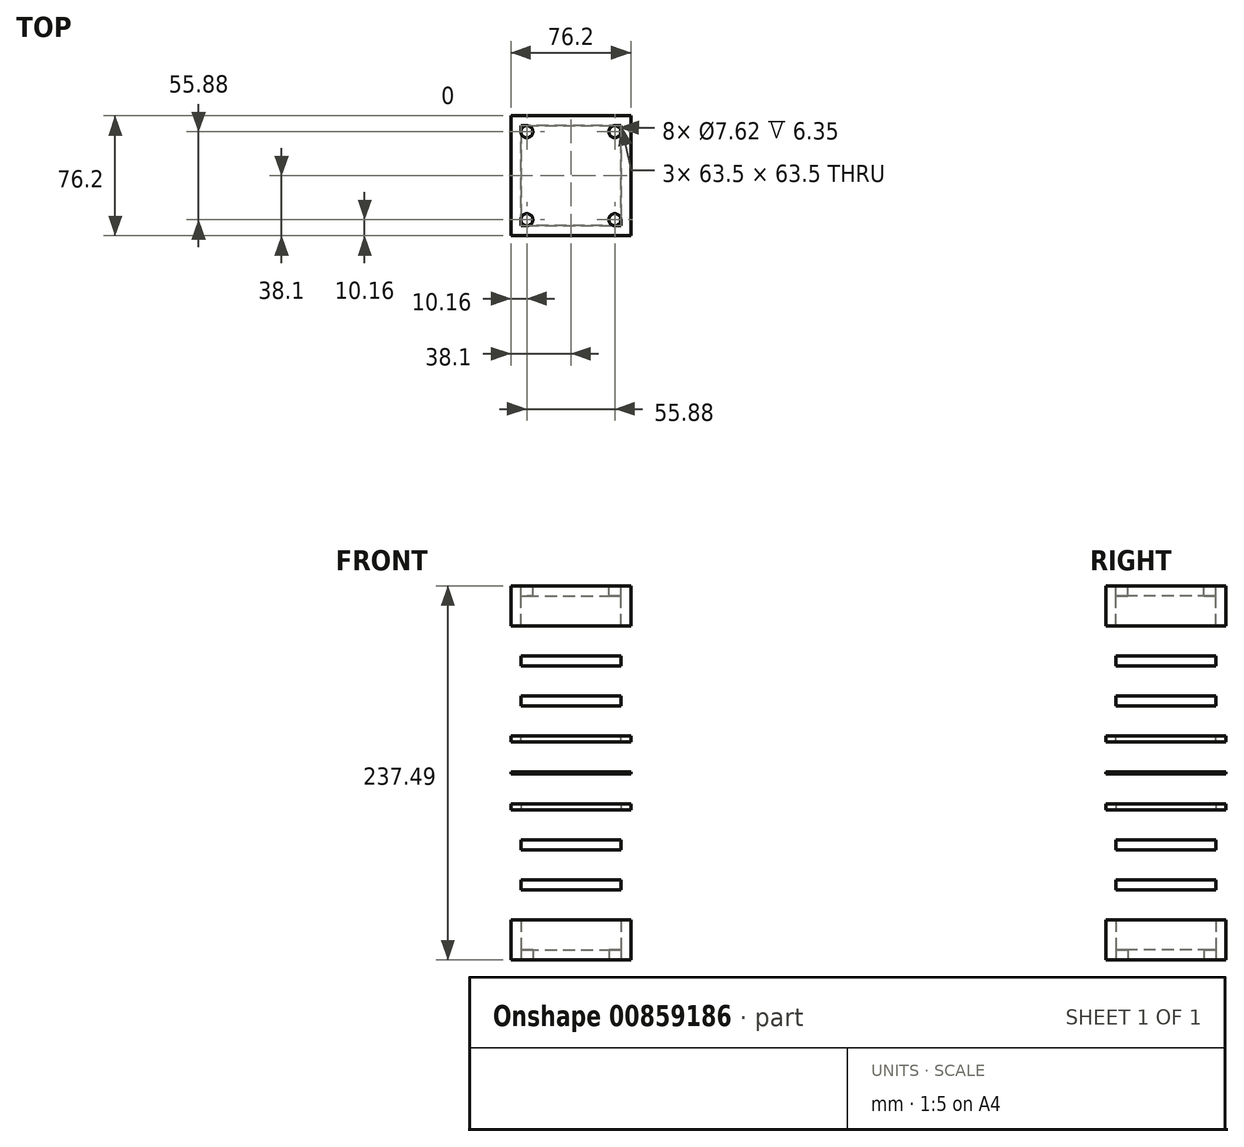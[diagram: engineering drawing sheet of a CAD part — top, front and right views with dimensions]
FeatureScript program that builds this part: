
annotation { "Feature Type Name" : "Feature", "Feature Type Description" : "" }
export const myFeature = defineFeature(function(context is Context, id is Id, definition is map)
    precondition{}
    {
        {
            var Q0;
            Q0=qCreatedBy(makeId("Top.planeOp"),FACE);
            var sketch = newSketch(context, id + "F0", { "sketchPlane" : qUnion([Q0])});
            skLineSegment(sketch, "E0.bottom", {"start": v(0, 0) * mm, "end": v(76.2, 0) * mm});
            skLineSegment(sketch, "E0.top", {"start": v(0, 76.2) * mm, "end": v(76.2, 76.2) * mm});
            skLineSegment(sketch, "E0.left", {"start": v(0, 0) * mm, "end": v(0, 76.2) * mm});
            skLineSegment(sketch, "E0.right", {"start": v(76.2, 0) * mm, "end": v(76.2, 76.2) * mm});
            skLineSegment(sketch, "E1.bottom", {"start": v(6.35, 69.85) * mm, "end": v(69.85, 69.85) * mm});
            skLineSegment(sketch, "E1.top", {"start": v(6.35, 6.35) * mm, "end": v(69.85, 6.35) * mm});
            skLineSegment(sketch, "E1.left", {"start": v(6.35, 69.85) * mm, "end": v(6.35, 6.35) * mm});
            skLineSegment(sketch, "E1.right", {"start": v(69.85, 69.85) * mm, "end": v(69.85, 6.35) * mm});
            skSolve(sketch);
        }
        {
            var Q0;
            Q0 = qSketchRegion(id + "F0", true);
            extrude(context, id + "F1", {"entities" : qUnion([Q0]), "depth" : 25.4 * mm, "offsetDistance" : 25.4 * mm});
        }
        {
            var Q0;
            Q0=makeQuery(id+"F0.imprint","IMPRINT",FACE,{"disambiguationData":[TD([[makeQuery(id+"F0.imprint","IMPRINT",EDGE,{"derivedFrom":sQuery(id+"F0.wireOp",EDGE,"E1.bottom")}),-1.0]])]});
            extrude(context, id + "F2", {"entities" : qUnion([Q0]), "operationType" : NewBodyOperationType.ADD, "depth" : 6.35 * mm, "offsetDistance" : 25.4 * mm});
        }
        {
            var Q0;
            Q0=makeQuery(id+"F1.opExtrude","CAP_FACE",FACE,{"disambiguationData":[OSD([sQuery(id+"F0.wireOp",EDGE,"E0.bottom"),sQuery(id+"F0.wireOp",EDGE,"E0.top"),sQuery(id+"F0.wireOp",EDGE,"E0.left"),sQuery(id+"F0.wireOp",EDGE,"E0.right"),sQuery(id+"F0.wireOp",EDGE,"E1.bottom"),sQuery(id+"F0.wireOp",EDGE,"E1.top"),sQuery(id+"F0.wireOp",EDGE,"E1.left"),sQuery(id+"F0.wireOp",EDGE,"E1.right")])],"isStart":false});
            var sketch = newSketch(context, id + "F3", { "sketchPlane" : qUnion([Q0])});
            skLineSegment(sketch, "E2.bottom", {"start": v(0, 76.2) * mm, "end": v(76.2, 76.2) * mm});
            skLineSegment(sketch, "E2.top", {"start": v(0, 0) * mm, "end": v(76.2, 0) * mm});
            skLineSegment(sketch, "E2.left", {"start": v(0, 76.2) * mm, "end": v(0, 0) * mm});
            skLineSegment(sketch, "E2.right", {"start": v(76.2, 76.2) * mm, "end": v(76.2, 0) * mm});
            skSolve(sketch);
        }
        {
            var Q0;
            Q0 = qSketchRegion(id + "F3", true);
            extrude(context, id + "F4", {"entities" : qUnion([Q0]), "depth" : 25.4 * mm, "offsetDistance" : 25.4 * mm});
        }
        {
            var Q0;
            Q0 = qSketchRegion(id + "F3", true);
            extrude(context, id + "F5", {"entities" : qUnion([Q0]), "operationType" : NewBodyOperationType.REMOVE, "depth" : 19.05 * mm, "offsetDistance" : 25.4 * mm});
        }
        {
            var Q0;
            Q0=makeQuery(id+"F4.opExtrude","CAP_FACE",FACE,{"disambiguationData":[OSD([sQuery(id+"F3.wireOp",EDGE,"E2.bottom"),sQuery(id+"F3.wireOp",EDGE,"E2.top"),sQuery(id+"F3.wireOp",EDGE,"E2.left"),sQuery(id+"F3.wireOp",EDGE,"E2.right")])],"isStart":false});
            var sketch = newSketch(context, id + "F6", { "sketchPlane" : qUnion([Q0])});
            skLineSegment(sketch, "E3.bottom", {"start": v(69.85, 6.35) * mm, "end": v(6.35, 6.35) * mm});
            skLineSegment(sketch, "E3.top", {"start": v(69.85, 69.85) * mm, "end": v(6.35, 69.85) * mm});
            skLineSegment(sketch, "E3.left", {"start": v(69.85, 6.35) * mm, "end": v(69.85, 69.85) * mm});
            skLineSegment(sketch, "E3.right", {"start": v(6.35, 6.35) * mm, "end": v(6.35, 69.85) * mm});
            skSolve(sketch);
        }
        {
            var Q0;
            Q0=makeQuery(id+"F6.imprint","IMPRINT",FACE,{"disambiguationData":[TD([[makeQuery(id+"F6.imprint","IMPRINT",EDGE,{"derivedFrom":sQuery(id+"F6.wireOp",EDGE,"E3.bottom")}),1.0]])]});
            extrude(context, id + "F7", {"entities" : qUnion([Q0]), "operationType" : NewBodyOperationType.REMOVE, "oppositeDirection" : true, "depth" : 25.4 * mm, "offsetDistance" : 25.4 * mm});
        }
        {
            var Q0;
            Q0=makeQuery(id+"F4.opExtrude","CAP_FACE",FACE,{"disambiguationData":[OSD([sQuery(id+"F3.wireOp",EDGE,"E2.bottom"),sQuery(id+"F3.wireOp",EDGE,"E2.top"),sQuery(id+"F3.wireOp",EDGE,"E2.left"),sQuery(id+"F3.wireOp",EDGE,"E2.right")])],"isStart":false});
            var sketch = newSketch(context, id + "F8", { "sketchPlane" : qUnion([Q0])});
            skLineSegment(sketch, "E4.bottom", {"start": v(69.85, 69.85) * mm, "end": v(6.35, 69.85) * mm});
            skLineSegment(sketch, "E4.top", {"start": v(69.85, 6.35) * mm, "end": v(6.35, 6.35) * mm});
            skLineSegment(sketch, "E4.left", {"start": v(69.85, 69.85) * mm, "end": v(69.85, 6.35) * mm});
            skLineSegment(sketch, "E4.right", {"start": v(6.35, 69.85) * mm, "end": v(6.35, 6.35) * mm});
            skLineSegment(sketch, "E5.left", {"start": v(69.85, 6.35) * mm, "end": v(69.85, 69.85) * mm});
            skLineSegment(sketch, "E5.right", {"start": v(6.35, 6.35) * mm, "end": v(6.35, 69.85) * mm});
            skSolve(sketch);
        }
        {
            var Q0;
            Q0 = qSketchRegion(id + "F8", true);
            extrude(context, id + "F9", {"entities" : qUnion([Q0]), "depth" : 25.4 * mm, "offsetDistance" : 25.4 * mm});
        }
        {
            var Q0;
            Q0 = qSketchRegion(id + "F8", true);
            extrude(context, id + "F10", {"entities" : qUnion([Q0]), "operationType" : NewBodyOperationType.REMOVE, "depth" : 19.05 * mm, "offsetDistance" : 25.4 * mm});
        }
        {
            var Q0;
            Q0=makeQuery(id+"F9.opExtrude","CAP_FACE",FACE,{"disambiguationData":[OSD([sQuery(id+"F8.wireOp",EDGE,"E4.top"),sQuery(id+"F8.wireOp",EDGE,"E4.bottom"),sQuery(id+"F8.wireOp",EDGE,"E5.left"),sQuery(id+"F8.wireOp",EDGE,"E5.right")])],"isStart":false});
            var sketch = newSketch(context, id + "F11", { "sketchPlane" : qUnion([Q0])});
            skLineSegment(sketch, "E6.bottom", {"start": v(0, 0) * mm, "end": v(76.2, 0) * mm});
            skLineSegment(sketch, "E6.top", {"start": v(0, 76.2) * mm, "end": v(76.2, 76.2) * mm});
            skLineSegment(sketch, "E6.left", {"start": v(0, 0) * mm, "end": v(0, 76.2) * mm});
            skLineSegment(sketch, "E6.right", {"start": v(76.2, 0) * mm, "end": v(76.2, 76.2) * mm});
            skLineSegment(sketch, "E7.bottom", {"start": v(6.35, 6.35) * mm, "end": v(69.85, 6.35) * mm});
            skLineSegment(sketch, "E7.top", {"start": v(6.35, 69.85) * mm, "end": v(69.85, 69.85) * mm});
            skLineSegment(sketch, "E7.left", {"start": v(6.35, 6.35) * mm, "end": v(6.35, 69.85) * mm});
            skLineSegment(sketch, "E7.right", {"start": v(69.85, 6.35) * mm, "end": v(69.85, 69.85) * mm});
            skSolve(sketch);
        }
        {
            var Q0;
            Q0 = qSketchRegion(id + "F11", true);
            extrude(context, id + "F12", {"entities" : qUnion([Q0]), "depth" : 22.86 * mm, "offsetDistance" : 25.4 * mm});
        }
        {
            var Q0;
            Q0 = qSketchRegion(id + "F11", true);
            extrude(context, id + "F13", {"entities" : qUnion([Q0]), "operationType" : NewBodyOperationType.REMOVE, "depth" : 19.05 * mm, "offsetDistance" : 25.4 * mm});
        }
        {
            var Q0;
            Q0=makeQuery(id+"F12.opExtrude","CAP_FACE",FACE,{"disambiguationData":[OSD([sQuery(id+"F11.wireOp",EDGE,"E6.bottom"),sQuery(id+"F11.wireOp",EDGE,"E6.top"),sQuery(id+"F11.wireOp",EDGE,"E6.left"),sQuery(id+"F11.wireOp",EDGE,"E6.right"),sQuery(id+"F11.wireOp",EDGE,"E7.bottom"),sQuery(id+"F11.wireOp",EDGE,"E7.top"),sQuery(id+"F11.wireOp",EDGE,"E7.left"),sQuery(id+"F11.wireOp",EDGE,"E7.right")])],"isStart":false});
            var sketch = newSketch(context, id + "F14", { "sketchPlane" : qUnion([Q0])});
            skLineSegment(sketch, "E8.bottom", {"start": v(0, 0) * mm, "end": v(76.2, 0) * mm});
            skLineSegment(sketch, "E8.top", {"start": v(0, 76.2) * mm, "end": v(76.2, 76.2) * mm});
            skLineSegment(sketch, "E8.left", {"start": v(0, 0) * mm, "end": v(0, 76.2) * mm});
            skLineSegment(sketch, "E8.right", {"start": v(76.2, 0) * mm, "end": v(76.2, 76.2) * mm});
            skSolve(sketch);
        }
        {
            var Q0;
            Q0 = qSketchRegion(id + "F14", true);
            extrude(context, id + "F15", {"entities" : qUnion([Q0]), "depth" : 20.32 * mm, "offsetDistance" : 25.4 * mm});
        }
        {
            var Q0;
            Q0 = qSketchRegion(id + "F14", true);
            extrude(context, id + "F16", {"entities" : qUnion([Q0]), "operationType" : NewBodyOperationType.REMOVE, "depth" : 19.05 * mm, "offsetDistance" : 25.4 * mm});
        }
        {
            var Q0;
            Q0=makeQuery(id+"F16.boolean.opBoolean","COPY",FACE,{"derivedFrom":makeQuery(id+"F16.opExtrude","CAP_FACE",FACE,{"disambiguationData":[OSD([sQuery(id+"F14.wireOp",EDGE,"E8.bottom"),sQuery(id+"F14.wireOp",EDGE,"E8.top"),sQuery(id+"F14.wireOp",EDGE,"E8.left"),sQuery(id+"F14.wireOp",EDGE,"E8.right")])],"isStart":false})});
            var Q1;
            Q1=makeQuery(id+"F15.opExtrude","CAP_FACE",FACE,{"disambiguationData":[OSD([sQuery(id+"F14.wireOp",EDGE,"E8.bottom"),sQuery(id+"F14.wireOp",EDGE,"E8.top"),sQuery(id+"F14.wireOp",EDGE,"E8.left"),sQuery(id+"F14.wireOp",EDGE,"E8.right")])],"isStart":false});
            cPlane(context, id + "F17", {"entities" : qUnion([Q0, Q1]), "cplaneType" : CPlaneType.MID_PLANE, "offset" : 25.4 * mm, "width" : 152.4 * mm, "height" : 152.4 * mm});
        }
        {
            var Q0;
            Q0=makeQuery(id+"F15.opExtrude","SWEPT_BODY",BODY,{"disambiguationData":[OSD([sQuery(id+"F14.wireOp",EDGE,"E8.bottom"),sQuery(id+"F14.wireOp",EDGE,"E8.top"),sQuery(id+"F14.wireOp",EDGE,"E8.left"),sQuery(id+"F14.wireOp",EDGE,"E8.right")])]});
            var Q1;
            Q1=makeQuery(id+"F12.opExtrude","SWEPT_BODY",BODY,{"disambiguationData":[OSD([sQuery(id+"F11.wireOp",EDGE,"E6.bottom"),sQuery(id+"F11.wireOp",EDGE,"E6.top"),sQuery(id+"F11.wireOp",EDGE,"E6.left"),sQuery(id+"F11.wireOp",EDGE,"E6.right"),sQuery(id+"F11.wireOp",EDGE,"E7.bottom"),sQuery(id+"F11.wireOp",EDGE,"E7.top"),sQuery(id+"F11.wireOp",EDGE,"E7.left"),sQuery(id+"F11.wireOp",EDGE,"E7.right")])]});
            var Q2;
            Q2=makeQuery(id+"F9.opExtrude","SWEPT_BODY",BODY,{"disambiguationData":[OSD([sQuery(id+"F8.wireOp",EDGE,"E4.top"),sQuery(id+"F8.wireOp",EDGE,"E4.bottom"),sQuery(id+"F8.wireOp",EDGE,"E5.left"),sQuery(id+"F8.wireOp",EDGE,"E5.right")])]});
            var Q3;
            Q3=makeQuery(id+"F4.opExtrude","SWEPT_BODY",BODY,{"disambiguationData":[OSD([sQuery(id+"F3.wireOp",EDGE,"E2.bottom"),sQuery(id+"F3.wireOp",EDGE,"E2.top"),sQuery(id+"F3.wireOp",EDGE,"E2.left"),sQuery(id+"F3.wireOp",EDGE,"E2.right")])]});
            var Q4;
            Q4=makeQuery(id+"F1.opExtrude","SWEPT_BODY",BODY,{"disambiguationData":[OSD([sQuery(id+"F0.wireOp",EDGE,"E0.bottom"),sQuery(id+"F0.wireOp",EDGE,"E0.top"),sQuery(id+"F0.wireOp",EDGE,"E0.left"),sQuery(id+"F0.wireOp",EDGE,"E0.right"),sQuery(id+"F0.wireOp",EDGE,"E1.bottom"),sQuery(id+"F0.wireOp",EDGE,"E1.top"),sQuery(id+"F0.wireOp",EDGE,"E1.left"),sQuery(id+"F0.wireOp",EDGE,"E1.right")])]});
            var Q5;
            Q5=qCreatedBy(id+"F17.planeOp",FACE);
            mirror(context, id + "F18", {"operationType" : NewBodyOperationType.ADD, "entities" : qUnion([Q0, Q1, Q2, Q3, Q4]), "mirrorPlane" : qUnion([Q5])});
        }
        {
            var Q0;
            {var subQ0=sQuery(id+"F0.wireOp",EDGE,"E1.right");var subQ1=sQuery(id+"F0.wireOp",EDGE,"E1.left");var subQ2=sQuery(id+"F0.wireOp",EDGE,"E1.top");var subQ3=sQuery(id+"F0.wireOp",EDGE,"E1.bottom");Q0=makeQuery(id+"F18.opPattern","COPY",FACE,{"derivedFrom":makeQuery(id+"F2.boolean.opBoolean","MERGE",FACE,{"derivedFrom":[makeQuery(id+"F1.opExtrude","CAP_FACE",FACE,{"disambiguationData":[OSD([sQuery(id+"F0.wireOp",EDGE,"E0.bottom"),sQuery(id+"F0.wireOp",EDGE,"E0.top"),sQuery(id+"F0.wireOp",EDGE,"E0.left"),sQuery(id+"F0.wireOp",EDGE,"E0.right"),subQ3,subQ2,subQ1,subQ0])],"isStart":true}),makeQuery(id+"F2.opExtrude","CAP_FACE",FACE,{"disambiguationData":[OSD([subQ3,subQ2,subQ1,subQ0])],"isStart":true})]}),"instanceName":"1"});}
            var sketch = newSketch(context, id + "F19", { "sketchPlane" : qUnion([Q0])});
            skCircle(sketch, "E9", {"center": v(10.16, 10.16) * mm, "radius": 3.81 * mm});
            skCircle(sketch, "E10", {"center": v(10.16, 66.04) * mm, "radius": 3.81 * mm});
            skCircle(sketch, "E11", {"center": v(66.04, 66.04) * mm, "radius": 3.81 * mm});
            skCircle(sketch, "E12", {"center": v(66.04, 10.16) * mm, "radius": 3.81 * mm});
            skSolve(sketch);
        }
        {
            var Q0;
            Q0 = qSketchRegion(id + "F19", true);
            extrude(context, id + "F20", {"entities" : qUnion([Q0]), "operationType" : NewBodyOperationType.REMOVE, "oppositeDirection" : true, "depth" : 25.4 * mm, "offsetDistance" : 25.4 * mm});
        }
        {
            var Q0;
            {var subQ0=sQuery(id+"F0.wireOp",EDGE,"E1.right");var subQ1=sQuery(id+"F0.wireOp",EDGE,"E1.left");var subQ2=sQuery(id+"F0.wireOp",EDGE,"E1.top");var subQ3=sQuery(id+"F0.wireOp",EDGE,"E1.bottom");Q0=makeQuery(id+"F2.boolean.opBoolean","MERGE",FACE,{"derivedFrom":[makeQuery(id+"F1.opExtrude","CAP_FACE",FACE,{"disambiguationData":[OSD([sQuery(id+"F0.wireOp",EDGE,"E0.bottom"),sQuery(id+"F0.wireOp",EDGE,"E0.top"),sQuery(id+"F0.wireOp",EDGE,"E0.left"),sQuery(id+"F0.wireOp",EDGE,"E0.right"),subQ3,subQ2,subQ1,subQ0])],"isStart":true}),makeQuery(id+"F2.opExtrude","CAP_FACE",FACE,{"disambiguationData":[OSD([subQ3,subQ2,subQ1,subQ0])],"isStart":true})]});}
            var sketch = newSketch(context, id + "F21", { "sketchPlane" : qUnion([Q0])});
            skCircle(sketch, "E13", {"center": v(66.04, -66.04) * mm, "radius": 3.81 * mm});
            skCircle(sketch, "E14", {"center": v(10.16, -66.04) * mm, "radius": 3.81 * mm});
            skCircle(sketch, "E15", {"center": v(66.04, -10.16) * mm, "radius": 3.81 * mm});
            skCircle(sketch, "E16", {"center": v(10.16, -10.16) * mm, "radius": 3.81 * mm});
            skSolve(sketch);
        }
        {
            var Q0;
            Q0 = qSketchRegion(id + "F21", true);
            extrude(context, id + "F22", {"entities" : qUnion([Q0]), "operationType" : NewBodyOperationType.REMOVE, "oppositeDirection" : true, "depth" : 25.4 * mm, "offsetDistance" : 25.4 * mm});
        }
    });
